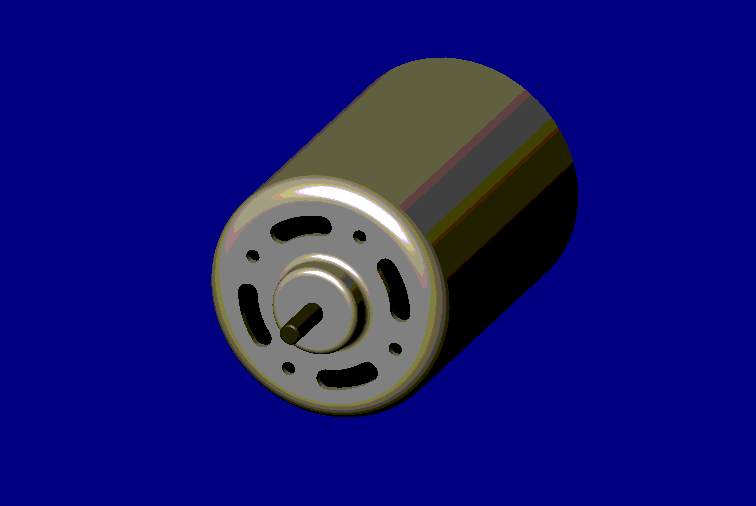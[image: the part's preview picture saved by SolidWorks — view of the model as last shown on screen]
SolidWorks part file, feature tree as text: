
SOLIDWORKS PART (.sldprt)
format: sldprt  version: not decoded by parser v0  size: 365,568 bytes
history: native  units: mm
features: sketch x10, extrude x6, plane x4, pattern_circular x4, shell x3, chamfer x2, material x1, fillet x1, cut_extrude x1 (+8 scaffold rows collapsed)
feature tree (40):
  scaffold x8  (default folders/planes/origin — collapsed)
  material  "Matériau <non spécifié>"
  plane  "Plane1"
  plane  "Plane2"
  plane  "Plane3"
  sketch  "Esquisse1"  dims[D1=36.0mm]
  extrude  "Base-Extrusion"  Depth=50mm
  fillet  "Congé1"  Radius=3mm
  shell  "Coque1"  Thickness=1mm
  sketch  "Esquisse2"  dims[D1=13.0mm]
  extrude  "Boss.-Extru.1"  Depth=4mm
  shell  "Congé2"  Thickness=1mm
  sketch  "Esquisse3"  dims[c1.D1=10.0mm c1.D2=13.0mm c1.D3=1.5mm c2.D1=18.0mm c3.D1=30.0deg]
  cut_extrude  "Enlèv. mat.-Extru.1"  [1 undecoded]
  pattern_circular  "Répétition circulaire1"  Count=4 Angle=90deg
  plane  "Plan1"  Offset=1mm
  sketch  "Esquisse4"
  extrude  "Boss.-Extru.2"  Depth=2mm
  sketch  "Esquisse5"  dims[D1=13.0mm]
  extrude  "Boss.-Extru.3"  Depth=3mm
  shell  "Congé3"  Thickness=1mm
  sketch  "Esquisse6"  dims[D1=3.0mm]
  extrude  "Boss.-Extru.4"  Depth=9mm
  chamfer  "Chanfrein1"  Distance=0.25mm Angle=45deg
  sketch  "Esquisse7"
  pattern_circular  "Enlèv. mat.-Extru.2"  [2 undecoded]
  sketch  "Esquisse8"  dims[D1=3.0mm]
  extrude  "Boss.-Extru.5"  Depth=3mm
  chamfer  "Chanfrein2"  Distance=0.25mm Angle=45deg
  sketch  "Esquisse9"
  pattern_circular  "Enlèv. mat.-Extru.3"  [2 undecoded]
  sketch  "Esquisse10"  dims[c1.D3=2.0mm c1.D1=19.0mm c2.D1=45.0deg c2.D2=12.0mm]
  pattern_circular  "Enlèv. mat.-Extru.4"  [2 undecoded]
decode coverage: 20 of 27 modeling features carry decoded parameters
note: 7 parameter values undecoded
note: suppression state not decoded; provenance and decode notes live in map.json
